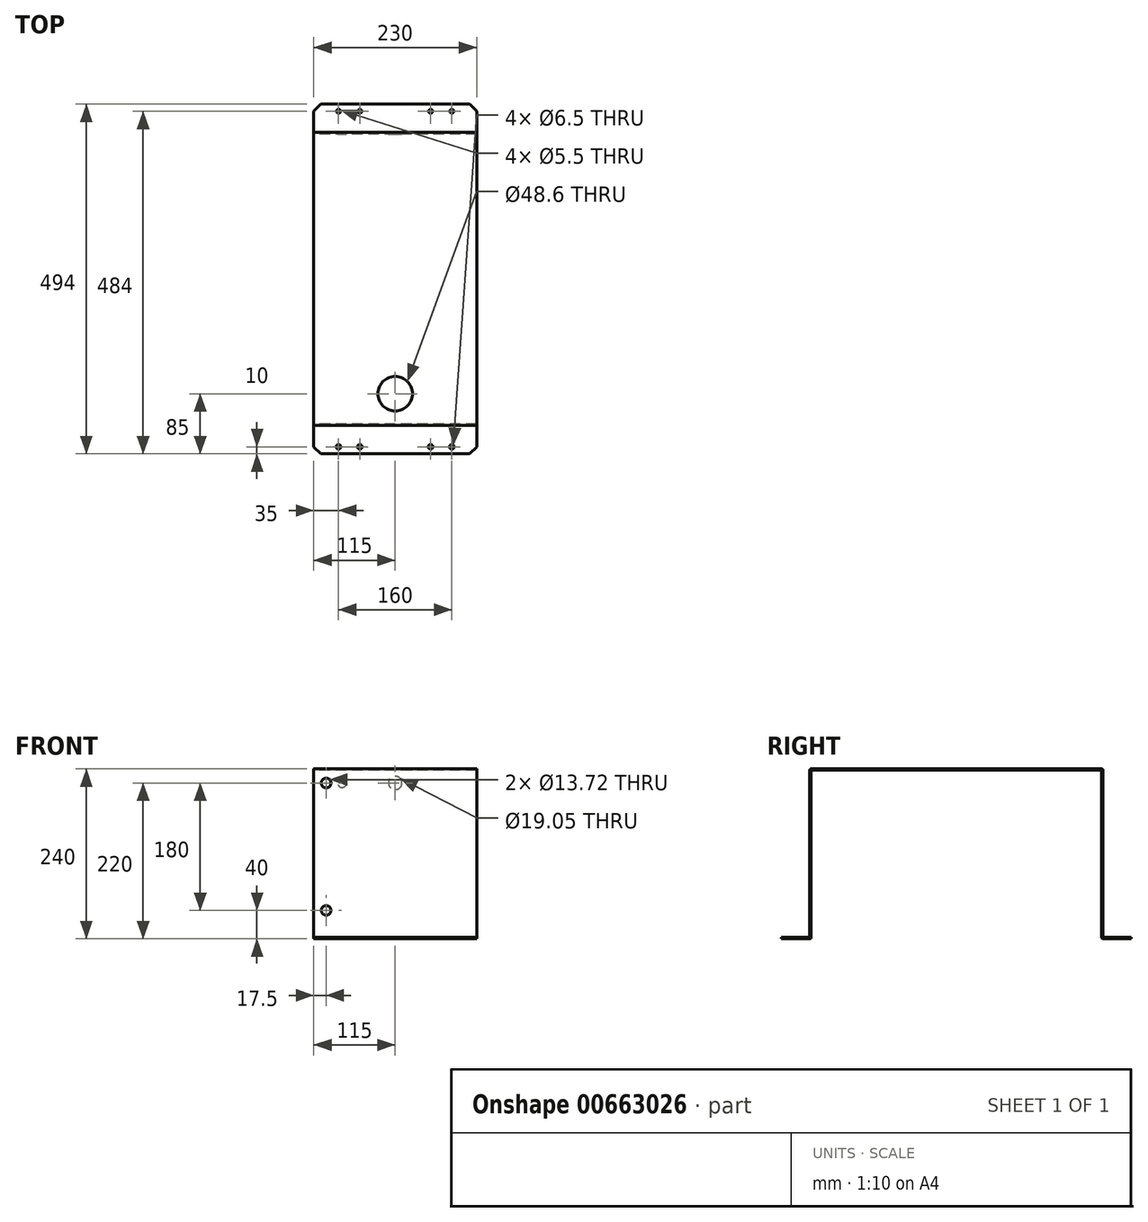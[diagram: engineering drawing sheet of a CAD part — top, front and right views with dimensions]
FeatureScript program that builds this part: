
annotation { "Feature Type Name" : "Feature", "Feature Type Description" : "" }
export const myFeature = defineFeature(function(context is Context, id is Id, definition is map)
    precondition{}
    {
        {
            var Q0;
            Q0=qCreatedBy(makeId("Right.planeOp"),FACE);
            var sketch = newSketch(context, id + "F0", { "sketchPlane" : qUnion([Q0])});
            skLineSegment(sketch, "E0", {"start": v(-205, 0) * mm, "end": v(205, 0) * mm});
            skLineSegment(sketch, "E1", {"start": v(207, -2) * mm, "end": v(207, -238) * mm});
            skLineSegment(sketch, "E2", {"start": v(-207, -2) * mm, "end": v(-207, -238) * mm});
            skLineSegment(sketch, "E3", {"start": v(-207, -238) * mm, "end": v(-247, -238) * mm});
            skLineSegment(sketch, "E4", {"start": v(207, -238) * mm, "end": v(247, -238) * mm});
            skLineSegment(sketch, "E5.0", {"start": v(207, -240) * mm, "end": v(247, -240) * mm});
            skLineSegment(sketch, "E5.1", {"start": v(-207, -240) * mm, "end": v(-247, -240) * mm});
            skLineSegment(sketch, "E5.2", {"start": v(-205, -2) * mm, "end": v(-205, -238) * mm});
            skLineSegment(sketch, "E5.3", {"start": v(-205, -2) * mm, "end": v(205, -2) * mm});
            skLineSegment(sketch, "E5.4", {"start": v(205, -2) * mm, "end": v(205, -238) * mm});
            skLineSegment(sketch, "E6", {"start": v(247, -238) * mm, "end": v(247, -240) * mm});
            skLineSegment(sketch, "E7", {"start": v(-247, -238) * mm, "end": v(-247, -240) * mm});
            skPoint(sketch, "E8.visualSharp", {"position": v(-207, 0) * mm});
            skArc(sketch, "E8.filletArc", {"start": v(-205, 0) * mm, "mid": v(-206.41, -0.59) * mm, "end": v(-207, -2) * mm});
            skPoint(sketch, "E9.visualSharp", {"position": v(207, 0) * mm});
            skArc(sketch, "E9.filletArc", {"start": v(207, -2) * mm, "mid": v(206.41, -0.59) * mm, "end": v(205, 0) * mm});
            skPoint(sketch, "E10.visualSharp", {"position": v(205, -240) * mm});
            skArc(sketch, "E10.filletArc", {"start": v(205, -238) * mm, "mid": v(205.59, -239.41) * mm, "end": v(207, -240) * mm});
            skPoint(sketch, "E11.visualSharp", {"position": v(-205, -240) * mm});
            skArc(sketch, "E11.filletArc", {"start": v(-207, -240) * mm, "mid": v(-205.59, -239.41) * mm, "end": v(-205, -238) * mm});
            skSolve(sketch);
        }
        {
            var Q0;
            Q0=makeQuery(id+"F0.imprint","IMPRINT",FACE,{"disambiguationData":[TD([[makeQuery(id+"F0.imprint","IMPRINT",EDGE,{"derivedFrom":sQuery(id+"F0.wireOp",EDGE,"E0")}),-1.0]])]});
            extrude(context, id + "F1", {"entities" : qUnion([Q0]), "depth" : 230 * mm, "offsetDistance" : 25 * mm});
        }
        {
            var Q0;
            Q0=makeQuery(id+"F1.opExtrude","SWEPT_FACE",FACE,{"disambiguationData":[OSD([sQuery(id+"F0.wireOp",EDGE,"E0")])]});
            var sketch = newSketch(context, id + "F2", { "sketchPlane" : qUnion([Q0])});
            skPoint(sketch, "E12", {"position": v(115, -162) * mm});
            skSolve(sketch);
        }
        {
            var Q0;
            Q0=sQuery(id+"F2.wireOp",VERTEX,"E12");
            var Q1;
            Q1=makeQuery(id+"F1.opExtrude","SWEPT_BODY",BODY,{"disambiguationData":[OSD([sQuery(id+"F0.wireOp",EDGE,"E0"),sQuery(id+"F0.wireOp",EDGE,"E1"),sQuery(id+"F0.wireOp",EDGE,"E2"),sQuery(id+"F0.wireOp",EDGE,"E3"),sQuery(id+"F0.wireOp",EDGE,"E4"),sQuery(id+"F0.wireOp",EDGE,"E5.0"),sQuery(id+"F0.wireOp",EDGE,"E5.1"),sQuery(id+"F0.wireOp",EDGE,"E5.2"),sQuery(id+"F0.wireOp",EDGE,"E5.3"),sQuery(id+"F0.wireOp",EDGE,"E5.4"),sQuery(id+"F0.wireOp",EDGE,"E6"),sQuery(id+"F0.wireOp",EDGE,"E7"),sQuery(id+"F0.wireOp",EDGE,"E8.filletArc"),sQuery(id+"F0.wireOp",EDGE,"E9.filletArc"),sQuery(id+"F0.wireOp",EDGE,"E10.filletArc"),sQuery(id+"F0.wireOp",EDGE,"E11.filletArc")])]});
            hole(context, id + "F3", {"style" : HoleStyle.SIMPLE, "endStyle" : HoleEndStyle.THROUGH, "holeDiameter" : 48.6 * mm, "majorDiameter" : 5 * mm, "isTappedThrough" : true, "tappedDepth" : 12 * mm, "tapClearance" : 3, "locations" : qUnion([Q0]), "scope" : qUnion([Q1])});
        }
        {
            var Q0;
            Q0=makeQuery(id+"F1.opExtrude","SWEPT_FACE",FACE,{"disambiguationData":[OSD([sQuery(id+"F0.wireOp",EDGE,"E3")])]});
            var sketch = newSketch(context, id + "F4", { "sketchPlane" : qUnion([Q0])});
            skPoint(sketch, "E13", {"position": v(35, -237) * mm});
            skPoint(sketch, "E14", {"position": v(65, -237) * mm});
            skPoint(sketch, "E15", {"position": v(165, -237) * mm});
            skPoint(sketch, "E16", {"position": v(195, -237) * mm});
            skPoint(sketch, "E17", {"position": v(35, 237) * mm});
            skPoint(sketch, "E18", {"position": v(65, 237) * mm});
            skPoint(sketch, "E19", {"position": v(165, 237) * mm});
            skPoint(sketch, "E20", {"position": v(195, 237) * mm});
            skSolve(sketch);
        }
        {
            var Q0;
            Q0=sQuery(id+"F4.wireOp",VERTEX,"E13");
            var Q1;
            Q1=sQuery(id+"F4.wireOp",VERTEX,"E14");
            var Q2;
            Q2=sQuery(id+"F4.wireOp",VERTEX,"E15");
            var Q3;
            Q3=sQuery(id+"F4.wireOp",VERTEX,"E16");
            var Q4;
            Q4=makeQuery(id+"F1.opExtrude","SWEPT_BODY",BODY,{"disambiguationData":[OSD([sQuery(id+"F0.wireOp",EDGE,"E0"),sQuery(id+"F0.wireOp",EDGE,"E1"),sQuery(id+"F0.wireOp",EDGE,"E2"),sQuery(id+"F0.wireOp",EDGE,"E3"),sQuery(id+"F0.wireOp",EDGE,"E4"),sQuery(id+"F0.wireOp",EDGE,"E5.0"),sQuery(id+"F0.wireOp",EDGE,"E5.1"),sQuery(id+"F0.wireOp",EDGE,"E5.2"),sQuery(id+"F0.wireOp",EDGE,"E5.3"),sQuery(id+"F0.wireOp",EDGE,"E5.4"),sQuery(id+"F0.wireOp",EDGE,"E6"),sQuery(id+"F0.wireOp",EDGE,"E7"),sQuery(id+"F0.wireOp",EDGE,"E8.filletArc"),sQuery(id+"F0.wireOp",EDGE,"E9.filletArc"),sQuery(id+"F0.wireOp",EDGE,"E10.filletArc"),sQuery(id+"F0.wireOp",EDGE,"E11.filletArc")])]});
            hole(context, id + "F5", {"style" : HoleStyle.SIMPLE, "endStyle" : HoleEndStyle.THROUGH, "holeDiameter" : 6.5 * mm, "majorDiameter" : 5 * mm, "isTappedThrough" : true, "tappedDepth" : 12 * mm, "tapClearance" : 3, "locations" : qUnion([Q0, Q1, Q2, Q3]), "scope" : qUnion([Q4])});
        }
        {
            var Q0;
            Q0=sQuery(id+"F4.wireOp",VERTEX,"E17");
            var Q1;
            Q1=sQuery(id+"F4.wireOp",VERTEX,"E18");
            var Q2;
            Q2=sQuery(id+"F4.wireOp",VERTEX,"E19");
            var Q3;
            Q3=sQuery(id+"F4.wireOp",VERTEX,"E20");
            var Q4;
            Q4=makeQuery(id+"F1.opExtrude","SWEPT_BODY",BODY,{"disambiguationData":[OSD([sQuery(id+"F0.wireOp",EDGE,"E0"),sQuery(id+"F0.wireOp",EDGE,"E1"),sQuery(id+"F0.wireOp",EDGE,"E2"),sQuery(id+"F0.wireOp",EDGE,"E3"),sQuery(id+"F0.wireOp",EDGE,"E4"),sQuery(id+"F0.wireOp",EDGE,"E5.0"),sQuery(id+"F0.wireOp",EDGE,"E5.1"),sQuery(id+"F0.wireOp",EDGE,"E5.2"),sQuery(id+"F0.wireOp",EDGE,"E5.3"),sQuery(id+"F0.wireOp",EDGE,"E5.4"),sQuery(id+"F0.wireOp",EDGE,"E6"),sQuery(id+"F0.wireOp",EDGE,"E7"),sQuery(id+"F0.wireOp",EDGE,"E8.filletArc"),sQuery(id+"F0.wireOp",EDGE,"E9.filletArc"),sQuery(id+"F0.wireOp",EDGE,"E10.filletArc"),sQuery(id+"F0.wireOp",EDGE,"E11.filletArc")])]});
            hole(context, id + "F6", {"style" : HoleStyle.SIMPLE, "endStyle" : HoleEndStyle.THROUGH, "holeDiameter" : 5.5 * mm, "majorDiameter" : 5 * mm, "isTappedThrough" : true, "tappedDepth" : 12 * mm, "tapClearance" : 3, "locations" : qUnion([Q0, Q1, Q2, Q3]), "scope" : qUnion([Q4])});
        }
        {
            var Q0;
            Q0=makeQuery(id+"F1.opExtrude","CAP_EDGE",EDGE,{"disambiguationData":[OSD([sQuery(id+"F0.wireOp",EDGE,"E7")])],"isStart":true});
            var Q1;
            Q1=makeQuery(id+"F1.opExtrude","CAP_EDGE",EDGE,{"disambiguationData":[OSD([sQuery(id+"F0.wireOp",EDGE,"E7")])],"isStart":false});
            var Q2;
            Q2=makeQuery(id+"F1.opExtrude","CAP_EDGE",EDGE,{"disambiguationData":[OSD([sQuery(id+"F0.wireOp",EDGE,"E6")])],"isStart":false});
            var Q3;
            Q3=makeQuery(id+"F1.opExtrude","CAP_EDGE",EDGE,{"disambiguationData":[OSD([sQuery(id+"F0.wireOp",EDGE,"E6")])],"isStart":true});
            chamfer(context, id + "F7", {"entities" : qUnion([Q0, Q1, Q2, Q3]), "width" : 10 * mm, "tangentPropagation" : true});
        }
        {
            var Q0;
            Q0=makeQuery(id+"F1.opExtrude","SWEPT_FACE",FACE,{"disambiguationData":[OSD([sQuery(id+"F0.wireOp",EDGE,"E2")])]});
            var sketch = newSketch(context, id + "F8", { "sketchPlane" : qUnion([Q0])});
            skPoint(sketch, "E21", {"position": v(17.5, -20) * mm});
            skPoint(sketch, "E22", {"position": v(17.5, -200) * mm});
            skSolve(sketch);
        }
        {
            var Q0;
            Q0=sQuery(id+"F8.wireOp",VERTEX,"E21");
            var Q1;
            Q1=sQuery(id+"F8.wireOp",VERTEX,"E22");
            var Q2;
            Q2=makeQuery(id+"F1.opExtrude","SWEPT_BODY",BODY,{"disambiguationData":[OSD([sQuery(id+"F0.wireOp",EDGE,"E0"),sQuery(id+"F0.wireOp",EDGE,"E1"),sQuery(id+"F0.wireOp",EDGE,"E2"),sQuery(id+"F0.wireOp",EDGE,"E3"),sQuery(id+"F0.wireOp",EDGE,"E4"),sQuery(id+"F0.wireOp",EDGE,"E5.0"),sQuery(id+"F0.wireOp",EDGE,"E5.1"),sQuery(id+"F0.wireOp",EDGE,"E5.2"),sQuery(id+"F0.wireOp",EDGE,"E5.3"),sQuery(id+"F0.wireOp",EDGE,"E5.4"),sQuery(id+"F0.wireOp",EDGE,"E6"),sQuery(id+"F0.wireOp",EDGE,"E7"),sQuery(id+"F0.wireOp",EDGE,"E8.filletArc"),sQuery(id+"F0.wireOp",EDGE,"E9.filletArc"),sQuery(id+"F0.wireOp",EDGE,"E10.filletArc"),sQuery(id+"F0.wireOp",EDGE,"E11.filletArc")])]});
            hole(context, id + "F9", {"style" : HoleStyle.SIMPLE, "endStyle" : HoleEndStyle.BLIND, "holeDiameter" : 13.72 * mm, "majorDiameter" : 5 * mm, "holeDepth" : 5 * mm, "isTappedThrough" : true, "tappedDepth" : 12 * mm, "tapClearance" : 3, "locations" : qUnion([Q0, Q1]), "scope" : qUnion([Q2])});
        }
        {
            var Q0;
            Q0=makeQuery(id+"F1.opExtrude","SWEPT_FACE",FACE,{"disambiguationData":[OSD([sQuery(id+"F0.wireOp",EDGE,"E1")])]});
            var sketch = newSketch(context, id + "F10", { "sketchPlane" : qUnion([Q0])});
            skPoint(sketch, "E23", {"position": v(-115, -20) * mm});
            skPoint(sketch, "E24", {"position": v(-40, -20) * mm});
            skSolve(sketch);
        }
        {
            var Q0;
            Q0=sQuery(id+"F10.wireOp",VERTEX,"E23");
            var Q1;
            Q1=makeQuery(id+"F1.opExtrude","SWEPT_BODY",BODY,{"disambiguationData":[OSD([sQuery(id+"F0.wireOp",EDGE,"E0"),sQuery(id+"F0.wireOp",EDGE,"E1"),sQuery(id+"F0.wireOp",EDGE,"E2"),sQuery(id+"F0.wireOp",EDGE,"E3"),sQuery(id+"F0.wireOp",EDGE,"E4"),sQuery(id+"F0.wireOp",EDGE,"E5.0"),sQuery(id+"F0.wireOp",EDGE,"E5.1"),sQuery(id+"F0.wireOp",EDGE,"E5.2"),sQuery(id+"F0.wireOp",EDGE,"E5.3"),sQuery(id+"F0.wireOp",EDGE,"E5.4"),sQuery(id+"F0.wireOp",EDGE,"E6"),sQuery(id+"F0.wireOp",EDGE,"E7"),sQuery(id+"F0.wireOp",EDGE,"E8.filletArc"),sQuery(id+"F0.wireOp",EDGE,"E9.filletArc"),sQuery(id+"F0.wireOp",EDGE,"E10.filletArc"),sQuery(id+"F0.wireOp",EDGE,"E11.filletArc")])]});
            hole(context, id + "F11", {"style" : HoleStyle.SIMPLE, "endStyle" : HoleEndStyle.BLIND, "holeDiameter" : 19.05 * mm, "majorDiameter" : 5 * mm, "holeDepth" : 5 * mm, "isTappedThrough" : true, "tappedDepth" : 12 * mm, "tapClearance" : 3, "locations" : qUnion([Q0]), "scope" : qUnion([Q1])});
        }
        {
            var Q0;
            Q0=sQuery(id+"F10.wireOp",VERTEX,"E24");
            var Q1;
            Q1=makeQuery(id+"F1.opExtrude","SWEPT_BODY",BODY,{"disambiguationData":[OSD([sQuery(id+"F0.wireOp",EDGE,"E0"),sQuery(id+"F0.wireOp",EDGE,"E1"),sQuery(id+"F0.wireOp",EDGE,"E2"),sQuery(id+"F0.wireOp",EDGE,"E3"),sQuery(id+"F0.wireOp",EDGE,"E4"),sQuery(id+"F0.wireOp",EDGE,"E5.0"),sQuery(id+"F0.wireOp",EDGE,"E5.1"),sQuery(id+"F0.wireOp",EDGE,"E5.2"),sQuery(id+"F0.wireOp",EDGE,"E5.3"),sQuery(id+"F0.wireOp",EDGE,"E5.4"),sQuery(id+"F0.wireOp",EDGE,"E6"),sQuery(id+"F0.wireOp",EDGE,"E7"),sQuery(id+"F0.wireOp",EDGE,"E8.filletArc"),sQuery(id+"F0.wireOp",EDGE,"E9.filletArc"),sQuery(id+"F0.wireOp",EDGE,"E10.filletArc"),sQuery(id+"F0.wireOp",EDGE,"E11.filletArc")])]});
            hole(context, id + "F12", {"style" : HoleStyle.SIMPLE, "endStyle" : HoleEndStyle.BLIND, "holeDiameter" : 12.7 * mm, "majorDiameter" : 5 * mm, "holeDepth" : 5 * mm, "isTappedThrough" : true, "tappedDepth" : 12 * mm, "tapClearance" : 3, "locations" : qUnion([Q0]), "scope" : qUnion([Q1])});
        }
    });
